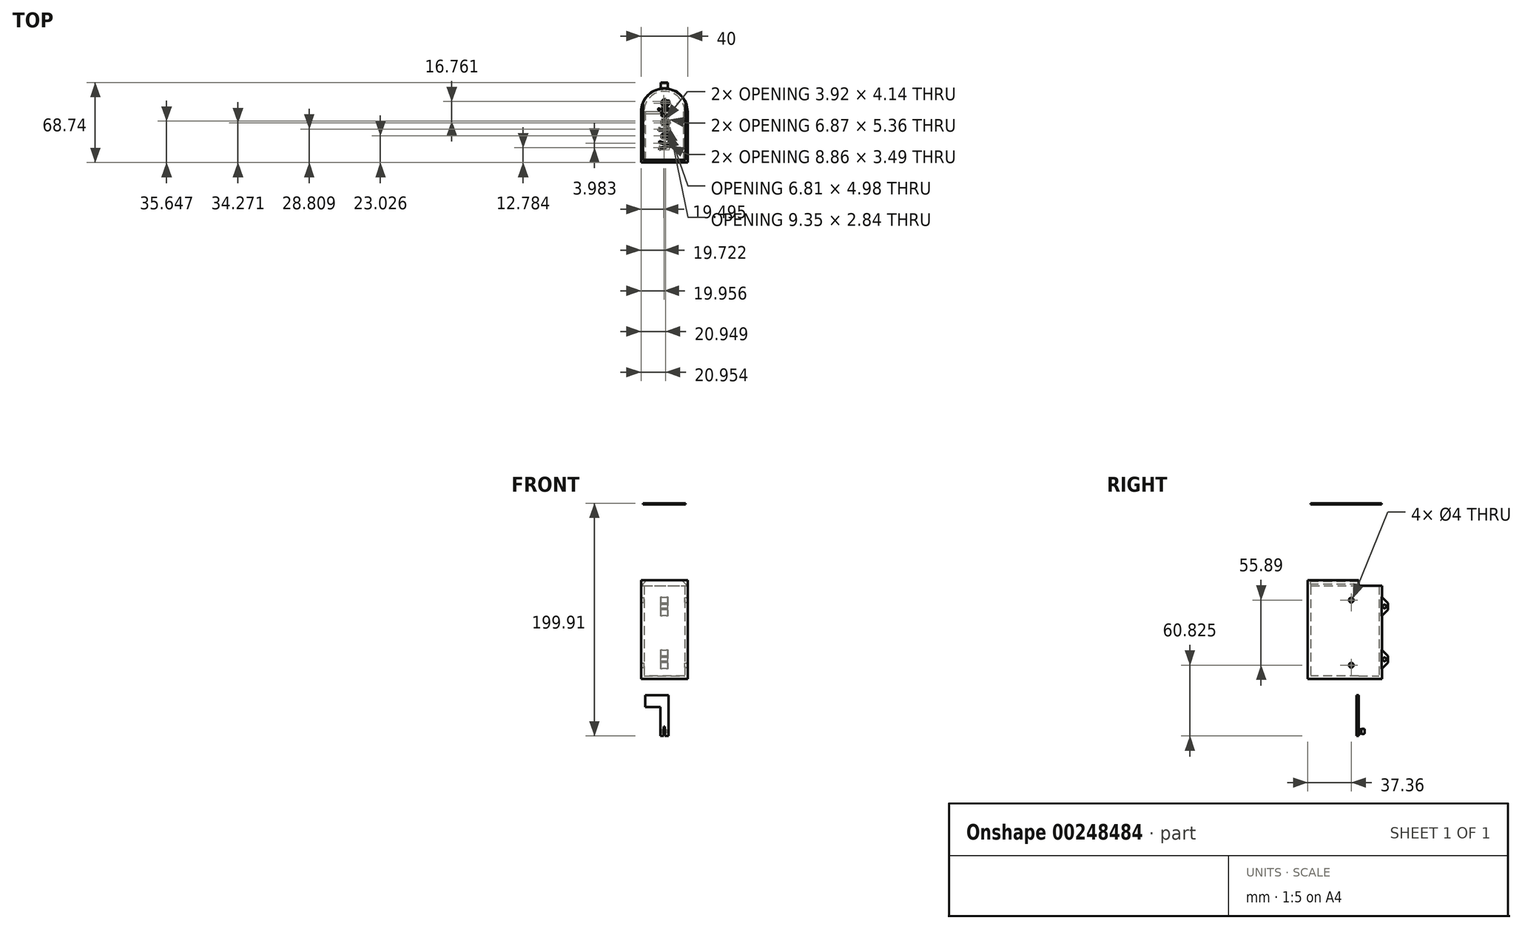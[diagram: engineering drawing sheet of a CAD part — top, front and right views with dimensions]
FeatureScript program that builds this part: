
annotation { "Feature Type Name" : "Feature", "Feature Type Description" : "" }
export const myFeature = defineFeature(function(context is Context, id is Id, definition is map)
    precondition{}
    {
        {
            var Q0;
            Q0=qCreatedBy(makeId("Top.planeOp"),FACE);
            var sketch = newSketch(context, id + "F0", { "sketchPlane" : qUnion([Q0])});
            skCircle(sketch, "E0", {"center": v(0, 0) * mm, "radius": 20 * mm});
            skLineSegment(sketch, "E1.bottom", {"start": v(-20, 0) * mm, "end": v(20, 0) * mm});
            skLineSegment(sketch, "E1.top", {"start": v(-20, -43.74) * mm, "end": v(20, -43.74) * mm});
            skLineSegment(sketch, "E1.left", {"start": v(-20, 0) * mm, "end": v(-20, -43.74) * mm});
            skLineSegment(sketch, "E1.right", {"start": v(20, 0) * mm, "end": v(20, -43.74) * mm});
            skSolve(sketch);
        }
        {
            var Q0;
            Q0=makeQuery(id+"F0.imprint","IMPRINT",FACE,{"disambiguationData":[TD([[makeQuery(id+"F0.imprint","IMPRINT",EDGE,{"derivedFrom":sQuery(id+"F0.wireOp",EDGE,"E1.top")}),1.0]])]});
            var Q1;
            {var subQ0=sQuery(id+"F0.wireOp",EDGE,"E1.bottom");Q1=makeQuery(id+"F0.imprint","IMPRINT",FACE,{"disambiguationData":[TD([[makeQuery(id+"F0.imprint","IMPRINT",EDGE,{"derivedFrom":subQ0}),-1.0]])]});}
            var Q2;
            {var subQ0=sQuery(id+"F0.wireOp",EDGE,"E1.bottom");Q2=makeQuery(id+"F0.imprint","IMPRINT",FACE,{"disambiguationData":[TD([[makeQuery(id+"F0.imprint","IMPRINT",EDGE,{"derivedFrom":subQ0}),1.0]])]});}
            extrude(context, id + "F1", {"entities" : qUnion([Q0, Q1, Q2]), "depth" : 85 * mm});
        }
        {
            var Q0;
            Q0=makeQuery(id+"F1.opExtrude","CAP_FACE",FACE,{"disambiguationData":[OSD([sQuery(id+"F0.wireOp",EDGE,"E0"),sQuery(id+"F0.wireOp",EDGE,"E1.top"),sQuery(id+"F0.wireOp",EDGE,"E1.left"),sQuery(id+"F0.wireOp",EDGE,"E1.right")])],"isStart":false});
            shell(context, id + "F2", {"entities" : qUnion([Q0]), "thickness" : 2.5 * mm});
        }
        {
            var Q0;
            Q0=qCreatedBy(makeId("Top.planeOp"),FACE);
            cPlane(context, id + "F3", {"entities" : qUnion([Q0]), "cplaneType" : CPlaneType.OFFSET, "offset" : 150 * mm, "width" : 150 * mm, "height" : 150 * mm});
        }
        {
            var Q0;
            Q0=makeQuery(id+"F1.opExtrude","SWEPT_FACE",FACE,{"disambiguationData":[OSD([sQuery(id+"F0.wireOp",EDGE,"E1.right")])]});
            var sketch = newSketch(context, id + "F4", { "sketchPlane" : qUnion([Q0])});
            skPoint(sketch, "E2", {"position": v(-6.38, 67.8) * mm});
            skPoint(sketch, "E3", {"position": v(-6.38, 11.92) * mm});
            skSolve(sketch);
        }
        {
            var Q0;
            Q0=sQuery(id+"F4.wireOp",VERTEX,"E2");
            var Q1;
            Q1=sQuery(id+"F4.wireOp",VERTEX,"E3");
            var Q2;
            Q2=makeQuery(id+"F1.opExtrude","SWEPT_BODY",BODY,{"disambiguationData":[OSD([sQuery(id+"F0.wireOp",EDGE,"E0"),sQuery(id+"F0.wireOp",EDGE,"E1.top"),sQuery(id+"F0.wireOp",EDGE,"E1.left"),sQuery(id+"F0.wireOp",EDGE,"E1.right")])]});
            hole(context, id + "F5", {"style" : HoleStyle.SIMPLE, "endStyle" : HoleEndStyle.THROUGH, "holeDiameter" : 4 * mm, "tappedDepth" : 12 * mm, "tapClearance" : 3, "startFromSketch" : true, "locations" : qUnion([Q0, Q1]), "scope" : qUnion([Q2])});
        }
        {
            var Q0;
            Q0=qCreatedBy(makeId("Front.planeOp"),FACE);
            var sketch = newSketch(context, id + "F6", { "sketchPlane" : qUnion([Q0])});
            skLineSegment(sketch, "E4.bottom", {"start": v(3.5, -23.9) * mm, "end": v(-3.5, -23.9) * mm});
            skLineSegment(sketch, "E4.top", {"start": v(3.5, -48.9) * mm, "end": v(-3.5, -48.9) * mm});
            skLineSegment(sketch, "E4.left", {"start": v(3.5, -23.9) * mm, "end": v(3.5, -48.9) * mm});
            skLineSegment(sketch, "E4.right", {"start": v(-3.5, -23.9) * mm, "end": v(-3.5, -48.9) * mm});
            skPoint(sketch, "E4.middle", {"position": v(0, -36.4) * mm});
            skLineSegment(sketch, "E5.bottom", {"start": v(3.5, -23.9) * mm, "end": v(-16.5, -23.9) * mm});
            skLineSegment(sketch, "E5.top", {"start": v(3.5, -13.9) * mm, "end": v(-16.5, -13.9) * mm});
            skLineSegment(sketch, "E5.left", {"start": v(3.5, -23.9) * mm, "end": v(3.5, -13.9) * mm});
            skLineSegment(sketch, "E5.right", {"start": v(-16.5, -23.9) * mm, "end": v(-16.5, -13.9) * mm});
            skSolve(sketch);
        }
        {
            var Q0;
            Q0=makeQuery(id+"F6.imprint","IMPRINT",FACE,{"disambiguationData":[TD([[makeQuery(id+"F6.imprint","IMPRINT",EDGE,{"derivedFrom":sQuery(id+"F6.wireOp",EDGE,"E5.top")}),1.0]])]});
            var Q1;
            Q1=makeQuery(id+"F6.imprint","IMPRINT",FACE,{"disambiguationData":[TD([[makeQuery(id+"F6.imprint","IMPRINT",EDGE,{"derivedFrom":sQuery(id+"F6.wireOp",EDGE,"E4.top")}),-1.0]])]});
            extrude(context, id + "F7", {"entities" : qUnion([Q0, Q1]), "depth" : 2 * mm});
        }
        {
            var Q0;
            Q0=qCreatedBy(makeId("Right.planeOp"),FACE);
            var sketch = newSketch(context, id + "F8", { "sketchPlane" : qUnion([Q0])});
            skLineSegment(sketch, "E6.bottom", {"start": v(0, -44.9) * mm, "end": v(4.97, -44.9) * mm});
            skLineSegment(sketch, "E6.top", {"start": v(0, -46.86) * mm, "end": v(4.97, -46.86) * mm});
            skLineSegment(sketch, "E6.left", {"start": v(0, -44.9) * mm, "end": v(0, -46.86) * mm});
            skLineSegment(sketch, "E6.right", {"start": v(4.97, -44.9) * mm, "end": v(4.97, -46.86) * mm});
            skLineSegment(sketch, "E7.0.1", {"start": v(0, -48.9) * mm, "end": v(-2, -48.9) * mm});
            skLineSegment(sketch, "E7.0.3", {"start": v(-2, -48.9) * mm, "end": v(0, -48.9) * mm});
            skPoint(sketch, "E8", {"position": v(2.3, -46.86) * mm});
            skArc(sketch, "E9", {"start": v(2.3, -46.86) * mm, "mid": v(3.63, -47.25) * mm, "end": v(4.97, -46.86) * mm});
            skSolve(sketch);
        }
        {
            var Q0;
            {var subQ0=sQuery(id+"F8.wireOp",EDGE,"E9");Q0=makeQuery(id+"F8.imprint","IMPRINT",FACE,{"disambiguationData":[TD([[makeQuery(id+"F8.imprint","IMPRINT",EDGE,{"derivedFrom":subQ0}),1.0]])]});}
            var Q1;
            Q1=makeQuery(id+"F8.imprint","IMPRINT",FACE,{"disambiguationData":[TD([[makeQuery(id+"F8.imprint","IMPRINT",EDGE,{"derivedFrom":sQuery(id+"F8.wireOp",EDGE,"E6.bottom")}),-1.0]])]});
            var Q2;
            Q2=sQuery(id+"F8.wireOp",EDGE,"E6.bottom");
            revolve(context, id + "F9", {"operationType" : NewBodyOperationType.ADD, "entities" : qUnion([Q0, Q1]), "axis" : qUnion([Q2]), "revolveType" : RevolveType.FULL});
        }
        {
            var Q0;
            Q0=makeQuery(id+"F9.opRevolve","SWEPT_FACE",FACE,{"disambiguationData":[OSD([sQuery(id+"F8.wireOp",EDGE,"E6.right")])]});
            var sketch = newSketch(context, id + "F10", { "sketchPlane" : qUnion([Q0])});
            skLineSegment(sketch, "E10.bottom", {"start": v(-0.5, -40.9) * mm, "end": v(0.5, -40.9) * mm});
            skLineSegment(sketch, "E10.top", {"start": v(-0.5, -48.9) * mm, "end": v(0.5, -48.9) * mm});
            skLineSegment(sketch, "E10.left", {"start": v(-0.5, -40.9) * mm, "end": v(-0.5, -48.9) * mm});
            skLineSegment(sketch, "E10.right", {"start": v(0.5, -40.9) * mm, "end": v(0.5, -48.9) * mm});
            skPoint(sketch, "E10.middle", {"position": v(0, -44.9) * mm});
            skSolve(sketch);
        }
        {
            var Q0;
            {var subQ0=sQuery(id+"F10.wireOp",EDGE,"E10.bottom");Q0=makeQuery(id+"F10.imprint","IMPRINT",FACE,{"disambiguationData":[TD([[makeQuery(id+"F10.imprint","IMPRINT",EDGE,{"derivedFrom":subQ0}),-1.0]])]});}
            var Q1;
            {var subQ0=sQuery(id+"F10.wireOp",EDGE,"E10.left");var subQ1=makeQuery(id+"F9.opRevolve","SWEPT_EDGE",EDGE,{"disambiguationData":[OSD([sQuery(id+"F8.wireOp",EDGE,"E6.top"),sQuery(id+"F8.wireOp",EDGE,"E6.right"),sQuery(id+"F8.wireOp",EDGE,"JZlQVU3P-cevF-KJDi-IWZO-h7zlHMFeMX4z")])]});var subQ2=makeQuery(id+"F10.imprint","INTERSECT",VERTEX,{"disambiguationData":[OD(0.0)],"derivedFrom":[subQ1,subQ0]});Q1=makeQuery(id+"F10.imprint","IMPRINT",FACE,{"disambiguationData":[TD([[makeQuery(id+"F10.imprint","IMPRINT",EDGE,{"disambiguationData":[TD([[subQ2,-1.0]])],"derivedFrom":subQ0}),1.0]])]});}
            var Q2;
            {var subQ0=sQuery(id+"F10.wireOp",EDGE,"E10.top");Q2=makeQuery(id+"F10.imprint","IMPRINT",FACE,{"disambiguationData":[TD([[makeQuery(id+"F10.imprint","IMPRINT",EDGE,{"derivedFrom":subQ0}),1.0]])]});}
            extrude(context, id + "F11", {"entities" : qUnion([Q0, Q1, Q2]), "operationType" : NewBodyOperationType.REMOVE, "endBound" : BoundingType.THROUGH_ALL, "oppositeDirection" : true, "depth" : 25 * mm});
        }
        {
            var Q0;
            Q0=makeQuery(id+"F2.opShell","OFFSET_FACE",FACE,{"disambiguationData":[OSD([sQuery(id+"F0.wireOp",EDGE,"E1.top")])]});
            var sketch = newSketch(context, id + "F12", { "sketchPlane" : qUnion([Q0])});
            skLineSegment(sketch, "E11.top", {"start": v(18.5, 80) * mm, "end": v(-18.5, 80) * mm});
            skLineSegment(sketch, "E11.left", {"start": v(18.5, 83) * mm, "end": v(18.5, 80) * mm});
            skLineSegment(sketch, "E11.right", {"start": v(-18.5, 83) * mm, "end": v(-18.5, 80) * mm});
            skLineSegment(sketch, "E12.0.1", {"start": v(-17.5, 2.5) * mm, "end": v(-17.5, 85) * mm});
            skLineSegment(sketch, "E12.0.3", {"start": v(-17.5, 85) * mm, "end": v(-17.5, 2.5) * mm});
            skLineSegment(sketch, "E13", {"start": v(18.5, 81.5) * mm, "end": v(17.5, 82.5) * mm});
            skLineSegment(sketch, "E14", {"start": v(-18.5, 81.5) * mm, "end": v(-17.5, 82.5) * mm});
            skLineSegment(sketch, "E15.0.0", {"start": v(-17.5, 2.5) * mm, "end": v(17.5, 2.5) * mm});
            skLineSegment(sketch, "E15.0.2", {"start": v(17.5, 85) * mm, "end": v(-17.5, 85) * mm});
            skLineSegment(sketch, "E15.0.3", {"start": v(-17.5, 85) * mm, "end": v(-17.5, 82.5) * mm});
            skPoint(sketch, "E16.orphan", {"position": v(17, 83) * mm});
            skPoint(sketch, "E17.orphan", {"position": v(-17, 83) * mm});
            skLineSegment(sketch, "E18.trimOffspring", {"start": v(17.5, 82.5) * mm, "end": v(17.5, 85) * mm});
            skSolve(sketch);
        }
        {
            var Q0;
            Q0 = qSketchRegion(id + "F12", true);
            extrude(context, id + "F13", {"entities" : qUnion([Q0]), "operationType" : NewBodyOperationType.REMOVE, "endBound" : BoundingType.THROUGH_ALL, "depth" : 25 * mm});
        }
        {
            var Q0;
            Q0=makeQuery(id+"F1.opExtrude","SWEPT_FACE",FACE,{"disambiguationData":[OSD([sQuery(id+"F0.wireOp",EDGE,"E1.right")])]});
            var sketch = newSketch(context, id + "F14", { "sketchPlane" : qUnion([Q0])});
            skLineSegment(sketch, "E19.0", {"start": v(7.6, 80) * mm, "end": v(20, 80) * mm});
            skLineSegment(sketch, "E20.bottom", {"start": v(0, 80) * mm, "end": v(32.85, 80) * mm});
            skLineSegment(sketch, "E20.top", {"start": v(0, 93.05) * mm, "end": v(32.85, 93.05) * mm});
            skLineSegment(sketch, "E20.left", {"start": v(0, 80) * mm, "end": v(0, 93.05) * mm});
            skLineSegment(sketch, "E20.right", {"start": v(32.85, 80) * mm, "end": v(32.85, 93.05) * mm});
            skSolve(sketch);
        }
        {
            var Q0;
            {var subQ6=sQuery(id+"F14.wireOp",EDGE,"E20.top");Q0=makeQuery(id+"F14.imprint","IMPRINT",FACE,{"disambiguationData":[TD([[makeQuery(id+"F14.imprint","IMPRINT",EDGE,{"derivedFrom":subQ6}),-1.0]])]});}
            extrude(context, id + "F15", {"entities" : qUnion([Q0]), "operationType" : NewBodyOperationType.REMOVE, "endBound" : BoundingType.THROUGH_ALL, "oppositeDirection" : true, "depth" : 25 * mm});
        }
        {
            var Q0;
            Q0=makeQuery(id+"F13.boolean.opBoolean","MERGE",FACE,{"derivedFrom":[makeQuery(id+"F2.opShell","OFFSET_FACE",FACE,{"disambiguationData":[OSD([sQuery(id+"F0.wireOp",EDGE,"E1.top")])]}),makeQuery(id+"F13.opExtrude","CAP_FACE",FACE,{"disambiguationData":[OSD([sQuery(id+"F12.wireOp",EDGE,"E11.top"),sQuery(id+"F12.wireOp",EDGE,"E11.left"),sQuery(id+"F12.wireOp",EDGE,"E11.right"),sQuery(id+"F12.wireOp",EDGE,"E13"),sQuery(id+"F12.wireOp",EDGE,"E14"),sQuery(id+"F12.wireOp",EDGE,"E15.0.2"),sQuery(id+"F12.wireOp",EDGE,"E15.0.3"),sQuery(id+"F12.wireOp",EDGE,"E18.trimOffspring")])],"isStart":true})]});
            var sketch = newSketch(context, id + "F16", { "sketchPlane" : qUnion([Q0])});
            skLineSegment(sketch, "E21.0", {"start": v(18.5, 81.5) * mm, "end": v(16.38, 83.62) * mm});
            skPoint(sketch, "E22.orphan", {"position": v(17.5, 82.5) * mm});
            skLineSegment(sketch, "E23", {"start": v(16.38, 83.62) * mm, "end": v(16.38, 85) * mm});
            skLineSegment(sketch, "E24", {"start": v(16.38, 85) * mm, "end": v(17.5, 85) * mm});
            skLineSegment(sketch, "E25", {"start": v(17.5, 85) * mm, "end": v(17.5, 82.5) * mm});
            skLineSegment(sketch, "E26", {"start": v(0, 79.3) * mm, "end": v(0, 94.97) * mm});
            skLineSegment(sketch, "E27.MirrorCS", {"start": v(-16.38, 83.62) * mm, "end": v(-16.38, 85) * mm});
            skLineSegment(sketch, "E28.MirrorCS", {"start": v(-18.5, 81.5) * mm, "end": v(-16.38, 83.62) * mm});
            skLineSegment(sketch, "E29.MirrorCS", {"start": v(-17.5, 85) * mm, "end": v(-17.5, 82.5) * mm});
            skLineSegment(sketch, "E30.MirrorCS", {"start": v(-16.38, 85) * mm, "end": v(-17.5, 85) * mm});
            skSolve(sketch);
        }
        {
            var Q0;
            {var subQ2=sQuery(id+"F16.wireOp",EDGE,"E23");Q0=makeQuery(id+"F16.imprint","IMPRINT",FACE,{"disambiguationData":[TD([[makeQuery(id+"F16.imprint","IMPRINT",EDGE,{"derivedFrom":subQ2}),-1.0]])]});}
            var Q1;
            {var subQ0=sQuery(id+"F16.wireOp",EDGE,"E27.MirrorCS");Q1=makeQuery(id+"F16.imprint","IMPRINT",FACE,{"disambiguationData":[TD([[makeQuery(id+"F16.imprint","IMPRINT",EDGE,{"derivedFrom":subQ0}),1.0]])]});}
            var Q2;
            {var subQ0=sQuery(id+"F0.wireOp",EDGE,"E1.right");Q2=makeQuery(id+"F15.boolean.opBoolean","COPY",FACE,{"disambiguationData":[TD([makeQuery(id+"F1.opExtrude","SWEPT_FACE",FACE,{"disambiguationData":[OSD([subQ0])]})])],"derivedFrom":makeQuery(id+"F15.opExtrude","SWEPT_FACE",FACE,{"disambiguationData":[OSD([sQuery(id+"F14.wireOp",EDGE,"E20.left")])]})});}
            extrude(context, id + "F17", {"entities" : qUnion([Q0, Q1]), "operationType" : NewBodyOperationType.ADD, "endBound" : BoundingType.UP_TO_SURFACE, "endBoundEntityFace" : qUnion([Q2]), "depth" : 25 * mm});
        }
        {
            var Q0;
            Q0=qCreatedBy(makeId("Right.planeOp"),FACE);
            var sketch = newSketch(context, id + "F18", { "sketchPlane" : qUnion([Q0])});
            skLineSegment(sketch, "E31", {"start": v(18, 6.93) * mm, "end": v(25, 13.93) * mm});
            skLineSegment(sketch, "E32", {"start": v(25, 13.93) * mm, "end": v(25, 19.93) * mm});
            skLineSegment(sketch, "E33", {"start": v(25, 19.93) * mm, "end": v(18, 26.93) * mm});
            skLineSegment(sketch, "E34", {"start": v(18, 26.93) * mm, "end": v(18, 6.93) * mm});
            skLineSegment(sketch, "E35", {"start": v(20, 80) * mm, "end": v(20, 0) * mm});
            skCircle(sketch, "E36", {"center": v(22.1, 16.93) * mm, "radius": 1.5 * mm});
            skLineSegment(sketch, "E37.0.1.0", {"start": v(18, 52.33) * mm, "end": v(25, 59.33) * mm});
            skLineSegment(sketch, "E37.0.1.1", {"start": v(25, 59.33) * mm, "end": v(25, 65.33) * mm});
            skLineSegment(sketch, "E37.0.1.2", {"start": v(25, 65.33) * mm, "end": v(18, 72.33) * mm});
            skLineSegment(sketch, "E37.0.1.3", {"start": v(18, 72.33) * mm, "end": v(18, 52.33) * mm});
            skCircle(sketch, "E37.0.1.4", {"center": v(22.1, 62.33) * mm, "radius": 1.5 * mm});
            skLineSegment(sketch, "E37.0.1.5", {"start": v(20, 125.4) * mm, "end": v(20, 45.4) * mm});
            skLineSegment(sketch, "E37.direction1", {"start": v(20, 0) * mm, "end": v(45, 0) * mm, "construction": true});
            skLineSegment(sketch, "E37.direction2", {"start": v(20, 0) * mm, "end": v(20, 45.4) * mm, "construction": true});
            skSolve(sketch);
        }
        {
            var Q0;
            Q0 = qSketchRegion(id + "F18", true);
            extrude(context, id + "F19", {"entities" : qUnion([Q0]), "operationType" : NewBodyOperationType.ADD, "depth" : 3 * mm, "hasSecondDirection" : true, "secondDirectionOppositeDirection" : true, "secondDirectionDepth" : 3 * mm});
        }
        {
            var Q0;
            Q0=qCreatedBy(id+"F3.planeOp",FACE);
            var sketch = newSketch(context, id + "F20", { "sketchPlane" : qUnion([Q0])});
            skLineSegment(sketch, "E38.0", {"start": v(18.5, 7.6) * mm, "end": v(18.5, -41.24) * mm});
            skLineSegment(sketch, "E39.0", {"start": v(-18.5, 7.6) * mm, "end": v(-18.5, -41.24) * mm});
            skLineSegment(sketch, "E40.0.0", {"start": v(-16.5, -41.24) * mm, "end": v(16.5, -41.24) * mm});
            skLineSegment(sketch, "E40.0.2", {"start": v(16.5, -41.24) * mm, "end": v(17.5, -41.24) * mm});
            skLineSegment(sketch, "E40.0.3", {"start": v(17.5, -41.24) * mm, "end": v(18.5, -41.24) * mm});
            skLineSegment(sketch, "E40.0.5", {"start": v(18.5, -41.24) * mm, "end": v(17.5, -41.24) * mm});
            skLineSegment(sketch, "E40.0.7", {"start": v(17.5, -41.24) * mm, "end": v(-17.5, -41.24) * mm});
            skLineSegment(sketch, "E40.0.9", {"start": v(-17.5, -41.24) * mm, "end": v(-18.5, -41.24) * mm});
            skLineSegment(sketch, "E40.0.11", {"start": v(-18.5, -41.24) * mm, "end": v(-17.5, -41.24) * mm});
            skLineSegment(sketch, "E40.0.12", {"start": v(-17.5, -41.24) * mm, "end": v(-16.5, -41.24) * mm});
            skArc(sketch, "E41.0.0", {"start": v(-20, 0) * mm, "mid": v(-19.36, 5) * mm, "end": v(-17.5, 9.68) * mm});
            skArc(sketch, "E41.0.2", {"start": v(-17.5, 9.68) * mm, "mid": v(-18.03, 8.66) * mm, "end": v(-18.5, 7.6) * mm});
            skArc(sketch, "E41.0.4", {"start": v(-18.5, 7.6) * mm, "mid": v(0, 20) * mm, "end": v(18.5, 7.6) * mm});
            skArc(sketch, "E41.0.6", {"start": v(18.5, 7.6) * mm, "mid": v(18.03, 8.66) * mm, "end": v(17.5, 9.68) * mm});
            skArc(sketch, "E41.0.8", {"start": v(17.5, 9.68) * mm, "mid": v(19.36, 5) * mm, "end": v(20, 0) * mm});
            skArc(sketch, "E41.0.10", {"start": v(20, 0) * mm, "mid": v(0, 20) * mm, "end": v(-20, 0) * mm});
            skLineSegment(sketch, "E42.0", {"start": v(-18.3, 7.56) * mm, "end": v(-18.3, -41.24) * mm});
            skArc(sketch, "E42.1", {"start": v(-18.3, 7.56) * mm, "mid": v(0, 19.8) * mm, "end": v(18.3, 7.56) * mm});
            skLineSegment(sketch, "E42.2", {"start": v(18.3, 7.56) * mm, "end": v(18.3, -41.24) * mm});
            skSolve(sketch);
        }
        {
            var Q0;
            {var subQ3=sQuery(id+"F20.wireOp",EDGE,"E40.0.7");Q0=makeQuery(id+"F20.imprint","IMPRINT",FACE,{"disambiguationData":[TD([[makeQuery(id+"F20.imprint","IMPRINT",EDGE,{"derivedFrom":subQ3}),-1.0]])]});}
            extrude(context, id + "F21", {"entities" : qUnion([Q0]), "depth" : 1 * mm});
        }
        {
            var Q0;
            Q0=makeQuery(id+"F21.opExtrude","CAP_FACE",FACE,{"disambiguationData":[OSD([sQuery(id+"F20.wireOp",EDGE,"E40.0.5"),sQuery(id+"F20.wireOp",EDGE,"E40.0.7"),sQuery(id+"F20.wireOp",EDGE,"E40.0.11"),sQuery(id+"F20.wireOp",EDGE,"E40.0.12"),sQuery(id+"F20.wireOp",EDGE,"E42.0"),sQuery(id+"F20.wireOp",EDGE,"E42.1"),sQuery(id+"F20.wireOp",EDGE,"E42.2")])],"isStart":false});
            var sketch = newSketch(context, id + "F22", { "sketchPlane" : qUnion([Q0])});
            skText(sketch, "E43", { "text": "Valerie", "fontName": "AllertaStencil-Regular.ttf"});
            const initialGuessF22  = {"E43": [0.00434, -0.03342, 0, 1, 0.00882]};
            skSetInitialGuess(sketch, initialGuessF22);
            skSolve(sketch);
        }
        {
            var Q0;
            Q0 = qSketchRegion(id + "F22", true);
            extrude(context, id + "F23", {"entities" : qUnion([Q0]), "operationType" : NewBodyOperationType.REMOVE, "endBound" : BoundingType.UP_TO_NEXT, "oppositeDirection" : true, "depth" : 25 * mm});
        }
    });
